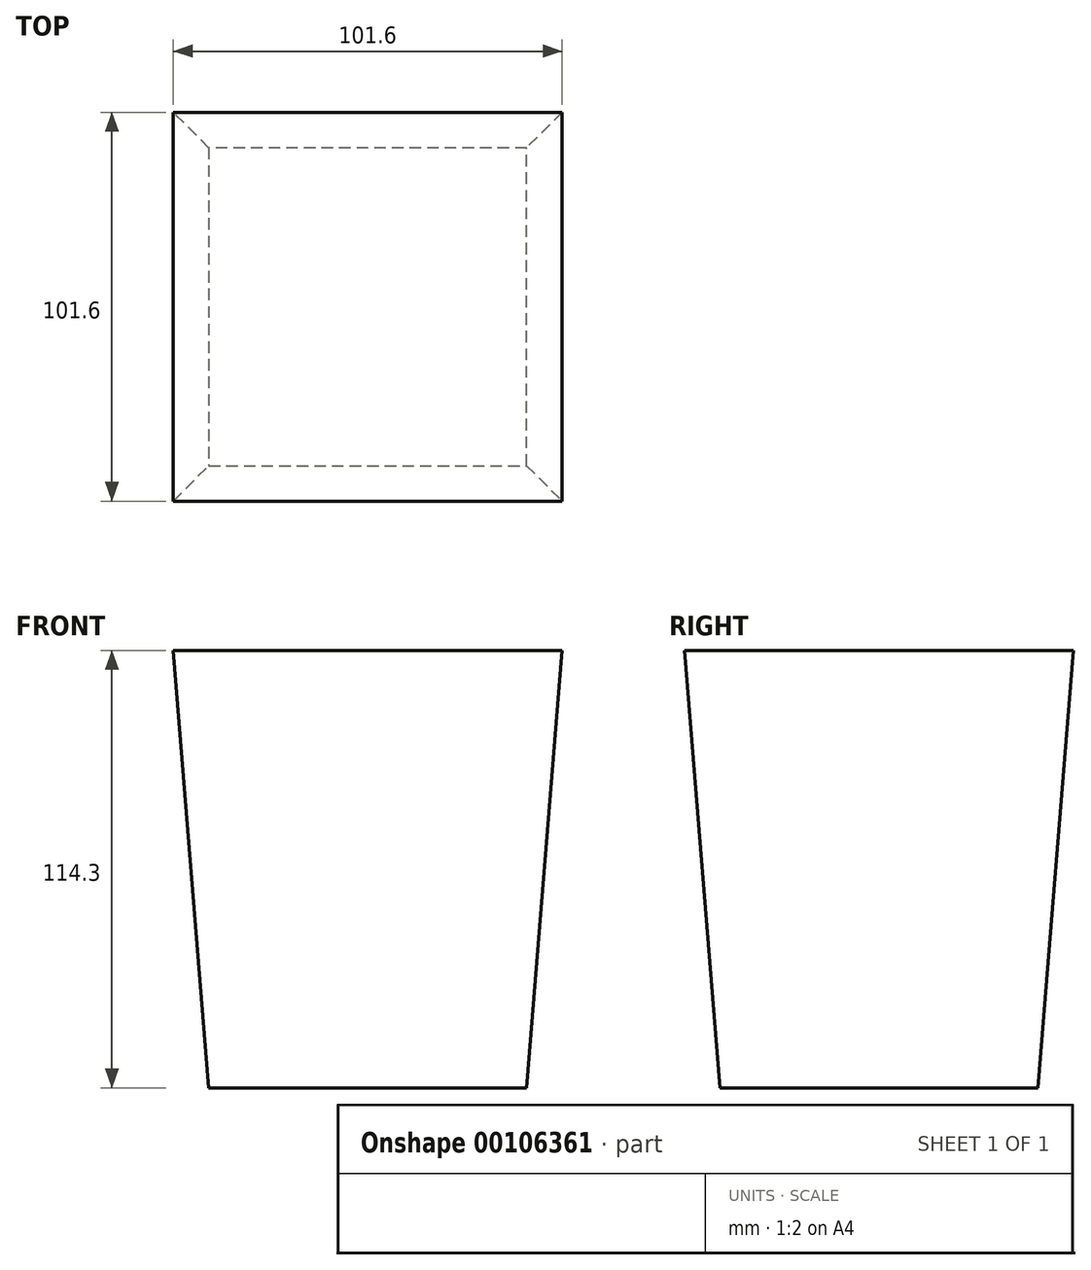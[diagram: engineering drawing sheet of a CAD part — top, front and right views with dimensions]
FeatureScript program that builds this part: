
annotation { "Feature Type Name" : "Feature", "Feature Type Description" : "" }
export const myFeature = defineFeature(function(context is Context, id is Id, definition is map)
    precondition{}
    {
        {
            var Q0;
            Q0=qCreatedBy(makeId("Top.planeOp"),FACE);
            var sketch = newSketch(context, id + "F0", { "sketchPlane" : qUnion([Q0])});
            skLineSegment(sketch, "E0.bottom", {"start": v(50.8, 50.8) * mm, "end": v(-50.8, 50.8) * mm});
            skLineSegment(sketch, "E0.top", {"start": v(50.8, -50.8) * mm, "end": v(-50.8, -50.8) * mm});
            skLineSegment(sketch, "E0.left", {"start": v(50.8, 50.8) * mm, "end": v(50.8, -50.8) * mm});
            skLineSegment(sketch, "E0.right", {"start": v(-50.8, 50.8) * mm, "end": v(-50.8, -50.8) * mm});
            skPoint(sketch, "E0.middle", {"position": v(0, 0) * mm});
            skSolve(sketch);
        }
        {
            var Q0;
            Q0 = qSketchRegion(id + "F0", true);
            extrude(context, id + "F1", {"entities" : qUnion([Q0]), "oppositeDirection" : true, "depth" : 114.3 * mm, "hasDraft" : true, "draftAngle" : 4.64 * degree, "draftPullDirection" : true});
        }
    });
